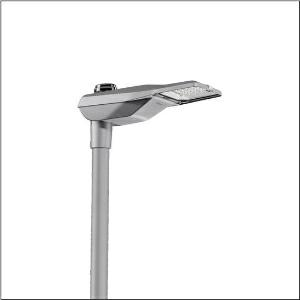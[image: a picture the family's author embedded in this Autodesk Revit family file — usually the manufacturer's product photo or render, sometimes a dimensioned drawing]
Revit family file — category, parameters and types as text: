
# Revit family: streetlight_sl_21_micro___st0_8a_5xe5c37n08cb_a39a
name_source: partatom
category: Lighting Fixtures
units: mm (PartAtom-declared; Revit-internal decimal feet)

## family parameters
Cut with Voids When Loaded = No
Host = Face
Light Source = No
Part Type = Normal
Room Calculation Point = No
Round Connector Dimension = Use Diameter
Shared = No

## types (1)
- --- (1 x LED, 2290 lm, 15.8 W, 3000K)
    Apparent Load = 16 VA
    CIE Flux Codes = 38 75 97 100 100
    Color Rendering = 70
    Color Temperature = 3000K
    Default Elevation = 1800 mm
    Description = Streetlight SL 21 micro, mast luminaire, primary light control with lens, of PMMA, primary optical cover: cover, of toughened safety glass, transparent, light distribution: ST0.8a, light emission: direct distribution, primary light characteristic: asymmetric, installation type: post-top, LED, 3G 1.5mm², High Power LED, rated luminous flux: 2.290lm, luminous efficacy: 145lm/W, light colour: 730, colour temperature: 3000K, control: overheat protection, pre-setting: linear dimming characteristic, constant luminous flux control, time-dependent luminous flux control, flexible luminous flux parameterisation, mains connection: 230..240V, AC, 50/60Hz, connection cable pre-assembled, cable length: 6,5m, wiring characteristics: H07RN-F, start of lifetime: 16W, end of service life: 16W, reduction: 8W, luminaire housing, of diecast aluminium (EN AC-44300), powder-coated, Siteco® metallic grey (DB 702S), corrosivity category C5 mid according to DIN EN ISO 12944, multi-level sealing system, sealing non-destructively replaceable, inclination adjustable: 0°, 5°, 10°, 15°, length: 528mm, width: 235mm, height: 110mm, spigot size: 76/60mm (post-top), protection rating (complete): IP66, insulation class (complete): insulation class I (protective earthing), certification: CE, ENEC, ENEC+, VDE, impact resistance: IK09, permissible operating ambient temperature for outdoor applications: -40..+50°C, standard-compliant lighting for roads and squares, packaging unit: 1 piece

Light Distribution: ST0.8a
    Height = 110 mm
    Lamp = 1 x LED
    Lamp Light Flux = 2290 lm
    Lamp Power = 15.8 W
    Lamp count = 1
    Length = 528 mm
    Luminous efficacy = 145 lm/W
    Manufacturer = Siteco
    ModVariant = No
    Model = 5XE5C37N08CB
    Number of Poles = 1
    OnlyDefault = Yes
    Power Factor = 1
    Product Name = Streetlight SL 21 micro | ST0.8a
    Product group = mast luminaire | pylon top
    ProductGroupID = 6100
    Protection Class = Protection class I
    Protection Degree = IP 66
    RLX_Detail_Level = 1
    RLX_Emergency_Light_Flux = 0 lm
    RLX_Emergency_Type = 0
    RLX_Emergency_Type_DB = No
    RlxData = <blob elided: 98333 chars, md5=e50aa1b6>
    Socket = socket
    Standby Power = 0 W
    System Light Flux = 2290 lm
    System Power = 16 W
    Type Comments = factory setting: luminous flux: 100 % | dim-lin: 254 | 300 mA
    Type Image = l_1294375.jpg
    URL = http://relux.com
    VarID = @adj_104215
    Voltage = 0 V
    Weight = 0.00 kg
    Width = 235 mm

## geometry (parser evidence)
native form markers: Blend x4, Sweep x10
no freeform markers — native parametric forms only
